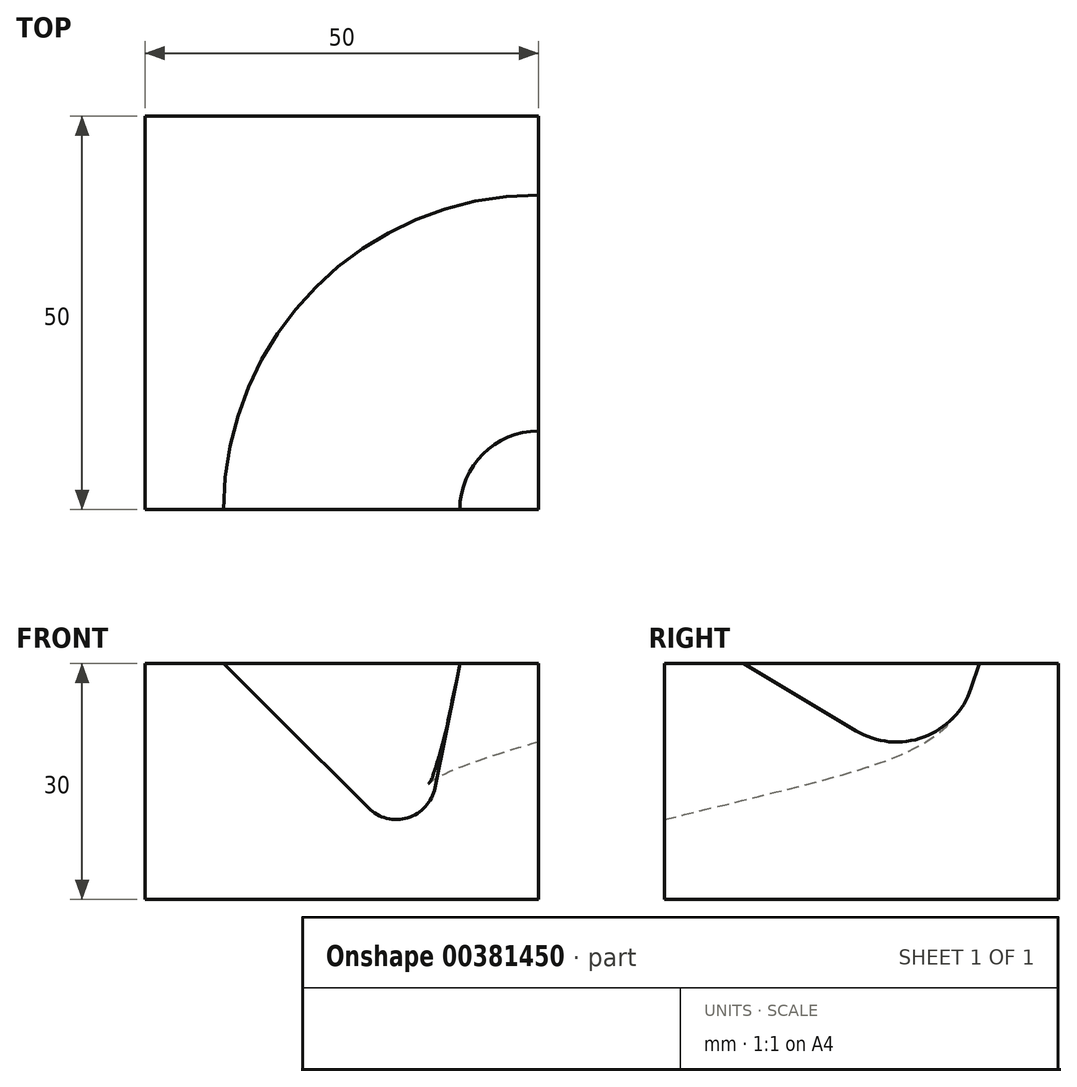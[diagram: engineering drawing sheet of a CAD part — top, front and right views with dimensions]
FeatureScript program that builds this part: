
annotation { "Feature Type Name" : "Feature", "Feature Type Description" : "" }
export const myFeature = defineFeature(function(context is Context, id is Id, definition is map)
    precondition{}
    {
        {
            var Q0;
            Q0=qCreatedBy(makeId("Top.planeOp"),FACE);
            var sketch = newSketch(context, id + "F0", { "sketchPlane" : qUnion([Q0])});
            skLineSegment(sketch, "E0.bottom", {"start": v(-25, 25) * mm, "end": v(25, 25) * mm});
            skLineSegment(sketch, "E0.top", {"start": v(-25, -25) * mm, "end": v(25, -25) * mm});
            skLineSegment(sketch, "E0.left", {"start": v(-25, 25) * mm, "end": v(-25, -25) * mm});
            skLineSegment(sketch, "E0.right", {"start": v(25, 25) * mm, "end": v(25, -25) * mm});
            skSolve(sketch);
        }
        {
            var Q0;
            Q0=makeQuery(id+"F0.imprint","IMPRINT",FACE,{"disambiguationData":[TD([[makeQuery(id+"F0.imprint","IMPRINT",EDGE,{"derivedFrom":sQuery(id+"F0.wireOp",EDGE,"E0.bottom")}),-1.0]])]});
            extrude(context, id + "F1", {"entities" : qUnion([Q0]), "depth" : 30 * mm});
        }
        {
            var Q0;
            Q0=makeQuery(id+"F1.opExtrude","CAP_FACE",FACE,{"disambiguationData":[OSD([sQuery(id+"F0.wireOp",EDGE,"E0.bottom"),sQuery(id+"F0.wireOp",EDGE,"E0.top"),sQuery(id+"F0.wireOp",EDGE,"E0.left"),sQuery(id+"F0.wireOp",EDGE,"E0.right")])],"isStart":false});
            var sketch = newSketch(context, id + "F2", { "sketchPlane" : qUnion([Q0])});
            skArc(sketch, "E1", {"start": v(25, 15) * mm, "mid": v(-3.28, 3.28) * mm, "end": v(-15, -25) * mm});
            skArc(sketch, "E2", {"start": v(25, -15) * mm, "mid": v(17.93, -17.93) * mm, "end": v(15, -25) * mm});
            skSolve(sketch);
        }
        {
            var Q0;
            Q0=makeQuery(id+"F1.opExtrude","SWEPT_FACE",FACE,{"disambiguationData":[OSD([sQuery(id+"F0.wireOp",EDGE,"E0.top")])]});
            var sketch = newSketch(context, id + "F3", { "sketchPlane" : qUnion([Q0])});
            skLineSegment(sketch, "E3", {"start": v(-15, 30) * mm, "end": v(3.4, 11.6) * mm});
            skLineSegment(sketch, "E4", {"start": v(11.83, 14.16) * mm, "end": v(15, 30) * mm});
            skPoint(sketch, "E5.visualSharp", {"position": v(10, 5) * mm});
            skArc(sketch, "E5.filletArc", {"start": v(3.4, 11.6) * mm, "mid": v(8.38, 10.36) * mm, "end": v(11.83, 14.16) * mm});
            skSolve(sketch);
        }
        {
            var Q0;
            Q0=makeQuery(id+"F1.opExtrude","SWEPT_FACE",FACE,{"disambiguationData":[OSD([sQuery(id+"F0.wireOp",EDGE,"E0.right")])]});
            var sketch = newSketch(context, id + "F4", { "sketchPlane" : qUnion([Q0])});
            skLineSegment(sketch, "E6", {"start": v(-15, 30) * mm, "end": v(-0.69, 21.41) * mm});
            skLineSegment(sketch, "E7", {"start": v(13.94, 26.83) * mm, "end": v(15, 30) * mm});
            skPoint(sketch, "E8.visualSharp", {"position": v(10, 15) * mm});
            skArc(sketch, "E8.filletArc", {"start": v(-0.69, 21.41) * mm, "mid": v(7.92, 20.6) * mm, "end": v(13.94, 26.83) * mm});
            skSolve(sketch);
        }
        {
            var Q1;
            {var subQ0=sQuery(id+"F3.wireOp",EDGE,"E3");Q1=makeQuery(id+"F3.imprint","IMPRINT",FACE,{"disambiguationData":[TD([[makeQuery(id+"F3.imprint","IMPRINT",EDGE,{"derivedFrom":subQ0}),1.0]])]});}
            var Q2;
            {var subQ0=sQuery(id+"F4.wireOp",EDGE,"E6");Q2=makeQuery(id+"F4.imprint","IMPRINT",FACE,{"disambiguationData":[TD([[makeQuery(id+"F4.imprint","IMPRINT",EDGE,{"derivedFrom":subQ0}),1.0]])]});}
            var Q3;
            Q3=sQuery(id+"F2.wireOp",EDGE,"E2");
            var Q4;
            Q4=sQuery(id+"F2.wireOp",EDGE,"E1");
            loft(context, id + "F5", {"operationType" : NewBodyOperationType.REMOVE, "addGuides" : true, "sheetProfilesArray" : [{ "sheetProfileEntities" : qUnion([Q1]) }, { "sheetProfileEntities" : qUnion([Q2]) }], "guidesArray" : [{ "guideEntities" : qUnion([Q3]), "guideDerivativeType" : LoftGuideDerivativeType.DEFAULT, "guideDerivativeMagnitude" : 1 }, { "guideEntities" : qUnion([Q4]), "guideDerivativeType" : LoftGuideDerivativeType.DEFAULT, "guideDerivativeMagnitude" : 1 }]});
        }
    });
